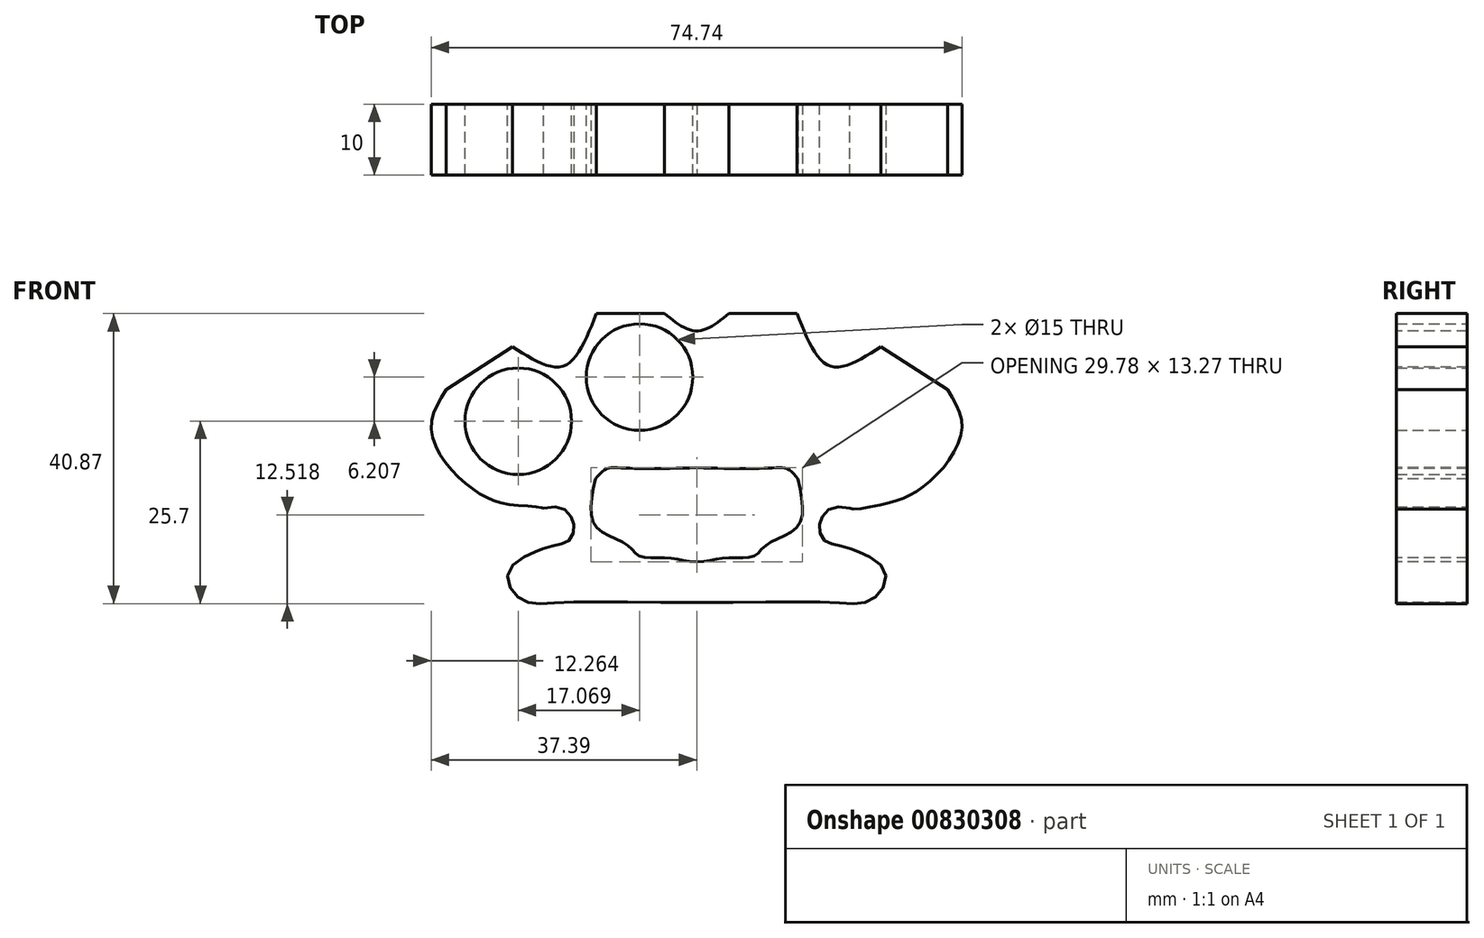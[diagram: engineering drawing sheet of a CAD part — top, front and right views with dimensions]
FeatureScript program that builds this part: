
annotation { "Feature Type Name" : "Feature", "Feature Type Description" : "" }
export const myFeature = defineFeature(function(context is Context, id is Id, definition is map)
    precondition{}
    {
        {
            var Q0;
            Q0=qCreatedBy(makeId("Front.planeOp"),FACE);
            var sketch = newSketch(context, id + "F0", { "sketchPlane" : qUnion([Q0])});
            skCircle(sketch, "E0", {"center": v(-25.13, 25.54) * mm, "radius": 7.5 * mm});
            skCircle(sketch, "E1", {"center": v(-8.06, 31.75) * mm, "radius": 7.5 * mm});
            skCircle(sketch, "E2.MirrorC", {"center": v(8.06, 31.75) * mm, "radius": 7.5 * mm});
            skCircle(sketch, "E3.MirrorC", {"center": v(25.13, 25.54) * mm, "radius": 7.5 * mm});
            skSolve(sketch);
        }
        {
            var Q0;
            Q0=qCreatedBy(makeId("Front.planeOp"),FACE);
            var sketch = newSketch(context, id + "F1", { "sketchPlane" : qUnion([Q0])});
            skLineSegment(sketch, "E4", {"start": v(-35.3, 29.96) * mm, "end": v(-25.94, 36.05) * mm});
            skLineSegment(sketch, "E5", {"start": v(-14.14, 40.71) * mm, "end": v(-4.54, 40.71) * mm});
            skLineSegment(sketch, "E6.MirrorCS", {"start": v(14.14, 40.71) * mm, "end": v(4.54, 40.71) * mm});
            skLineSegment(sketch, "E7.MirrorCS", {"start": v(35.3, 29.96) * mm, "end": v(25.94, 36.05) * mm});
            skFitSpline(sketch, "E8", {"points": [v(-25.94, 36.05) * mm, v(-18.8, 33.3) * mm, v(-14.14, 40.71) * mm], "startDerivative": vector(16.15, -10.51) * mm, "endDerivative": vector(7.54, 19.5) * mm});
            skFitSpline(sketch, "E9", {"points": [v(-4.54, 40.71) * mm, v(0, 38.24) * mm, v(4.54, 40.71) * mm], "startDerivative": vector(9.08, -7.4) * mm, "endDerivative": vector(9.08, 7.4) * mm});
            skFitSpline(sketch, "E10.MirrorCS", {"points": [v(25.94, 36.05) * mm, v(18.8, 33.3) * mm, v(14.14, 40.71) * mm], "startDerivative": vector(-16.15, -10.51) * mm, "endDerivative": vector(-7.54, 19.5) * mm});
            skFitSpline(sketch, "E11", {"points": [v(-35.3, 29.96) * mm, v(-37.38, 25.06) * mm, v(-35.3, 19.63) * mm, v(-30.6, 15.36) * mm, v(-26.32, 13.81) * mm, v(-21.69, 13.27) * mm, v(-21.53, 13.27) * mm], "startDerivative": vector(-15.86, -25.4) * mm, "endDerivative": vector(-0.38, 11.05) * mm});
            skFitSpline(sketch, "E12.MirrorCS", {"points": [v(35.3, 29.96) * mm, v(37.34, 25.12) * mm, v(35.26, 19.69) * mm, v(30.55, 15.42) * mm, v(26.28, 13.87) * mm, v(21.53, 13.27) * mm], "startDerivative": vector(15.86, -25.4) * mm, "endDerivative": vector(-5.2, 5.64) * mm});
            skFitSpline(sketch, "E13", {"points": [v(-21.53, 13.27) * mm, v(-18.91, 13.27) * mm, v(-17.54, 11.76) * mm, v(-17.27, 10.4) * mm, v(-17.95, 8.74) * mm, v(-19.33, 8.2) * mm, v(-21.53, 7.65) * mm, v(-23.17, 6.96) * mm, v(-26.32, 4.77) * mm, v(-26.05, 1.75) * mm, v(-23.58, 0) * mm, v(-19.33, 0) * mm, v(0, 0) * mm], "startDerivative": vector(37.82, 6.42) * mm, "endDerivative": vector(120.65, 0) * mm});
            skFitSpline(sketch, "E14.MirrorCS", {"points": [v(21.53, 13.27) * mm, v(18.91, 13.27) * mm, v(17.54, 11.76) * mm, v(17.27, 10.4) * mm, v(17.95, 8.74) * mm, v(19.33, 8.2) * mm, v(21.53, 7.65) * mm, v(23.17, 6.96) * mm, v(26.32, 4.77) * mm, v(26.05, 1.75) * mm, v(23.58, 0) * mm, v(19.33, 0) * mm, v(0, 0) * mm], "startDerivative": vector(-37.82, 6.42) * mm, "endDerivative": vector(-120.65, 0) * mm});
            skSolve(sketch);
        }
        {
            var Q0;
            Q0=makeQuery(id+"F1.imprint","IMPRINT",FACE,{"disambiguationData":[TD([[makeQuery(id+"F1.imprint","IMPRINT",EDGE,{"derivedFrom":sQuery(id+"F1.wireOp",EDGE,"E4")}),-1.0]])]});
            extrude(context, id + "F2", {"entities" : qUnion([Q0]), "endBound" : BoundingType.SYMMETRIC, "depth" : 10 * mm, "offsetDistance" : 25 * mm});
        }
        {
            var Q0;
            Q0=makeQuery(id+"F0.imprint","IMPRINT",FACE,{"disambiguationData":[TD([[makeQuery(id+"F0.imprint","IMPRINT",EDGE,{"derivedFrom":sQuery(id+"F0.wireOp",EDGE,"E1")}),1.0]])]});
            var Q1;
            Q1=makeQuery(id+"F0.imprint","IMPRINT",FACE,{"disambiguationData":[TD([[makeQuery(id+"F0.imprint","IMPRINT",EDGE,{"derivedFrom":sQuery(id+"F0.wireOp",EDGE,"E0")}),1.0]])]});
            var Q2;
            Q2=makeQuery(id+"F0.imprint","IMPRINT",FACE,{"disambiguationData":[TD([[makeQuery(id+"F0.imprint","IMPRINT",EDGE,{"derivedFrom":sQuery(id+"F0.wireOp",EDGE,"E2.MirrorC")}),-1.0]])]});
            var Q3;
            Q3=makeQuery(id+"F0.imprint","IMPRINT",FACE,{"disambiguationData":[TD([[makeQuery(id+"F0.imprint","IMPRINT",EDGE,{"derivedFrom":sQuery(id+"F0.wireOp",EDGE,"E3.MirrorC")}),-1.0]])]});
            extrude(context, id + "F3", {"entities" : qUnion([Q0, Q1, Q2, Q3]), "operationType" : NewBodyOperationType.REMOVE, "endBound" : BoundingType.SYMMETRIC, "depth" : 70.6 * mm, "offsetDistance" : 25 * mm});
        }
        {
            var Q0;
            Q0=makeQuery(id+"F2.opExtrude","CAP_FACE",FACE,{"disambiguationData":[OSD([sQuery(id+"F1.wireOp",EDGE,"E4"),sQuery(id+"F1.wireOp",EDGE,"E5"),sQuery(id+"F1.wireOp",EDGE,"E6.MirrorCS"),sQuery(id+"F1.wireOp",EDGE,"E7.MirrorCS"),sQuery(id+"F1.wireOp",EDGE,"E8"),sQuery(id+"F1.wireOp",EDGE,"E9"),sQuery(id+"F1.wireOp",EDGE,"E10.MirrorCS"),sQuery(id+"F1.wireOp",EDGE,"E11"),sQuery(id+"F1.wireOp",EDGE,"E12.MirrorCS"),sQuery(id+"F1.wireOp",EDGE,"E13"),sQuery(id+"F1.wireOp",EDGE,"E14.MirrorCS")])],"isStart":false});
            var sketch = newSketch(context, id + "F4", { "sketchPlane" : qUnion([Q0])});
            skFitSpline(sketch, "E15", {"points": [v(-14.27, 17.42) * mm, v(-14.27, 10.77) * mm, v(-9.99, 8.24) * mm, v(-7.94, 6.5) * mm, v(-3.98, 6.3) * mm, v(0.03, 5.72) * mm], "startDerivative": vector(-6.7, -32.29) * mm, "endDerivative": vector(23.65, 0.23) * mm});
            skFitSpline(sketch, "E16", {"points": [v(-14.27, 17.42) * mm, v(-12.9, 18.76) * mm, v(-11.63, 19) * mm, v(-8.05, 18.88) * mm, v(0, 19) * mm], "startDerivative": vector(7.19, 8.5) * mm, "endDerivative": vector(22.21, 0.6) * mm});
            skFitSpline(sketch, "E17.MirrorCS", {"points": [v(14.27, 17.42) * mm, v(12.9, 18.76) * mm, v(11.63, 19) * mm, v(8.05, 18.88) * mm, v(0, 19) * mm], "startDerivative": vector(-7.19, 8.5) * mm, "endDerivative": vector(-22.21, 0.6) * mm});
            skFitSpline(sketch, "E18.MirrorCS", {"points": [v(14.27, 17.42) * mm, v(14.27, 10.77) * mm, v(9.99, 8.24) * mm, v(7.94, 6.5) * mm, v(3.98, 6.3) * mm, v(-0.03, 5.72) * mm], "startDerivative": vector(6.7, -32.29) * mm, "endDerivative": vector(-23.65, 0.23) * mm});
            skSolve(sketch);
        }
        {
            var Q0;
            {var subQ0=sQuery(id+"F4.wireOp",EDGE,"E16");Q0=makeQuery(id+"F4.imprint","IMPRINT",FACE,{"disambiguationData":[TD([[makeQuery(id+"F4.imprint","IMPRINT",EDGE,{"derivedFrom":subQ0}),-1.0]])]});}
            extrude(context, id + "F5", {"entities" : qUnion([Q0]), "operationType" : NewBodyOperationType.REMOVE, "oppositeDirection" : true, "depth" : 25 * mm, "offsetDistance" : 25 * mm});
        }
    });
